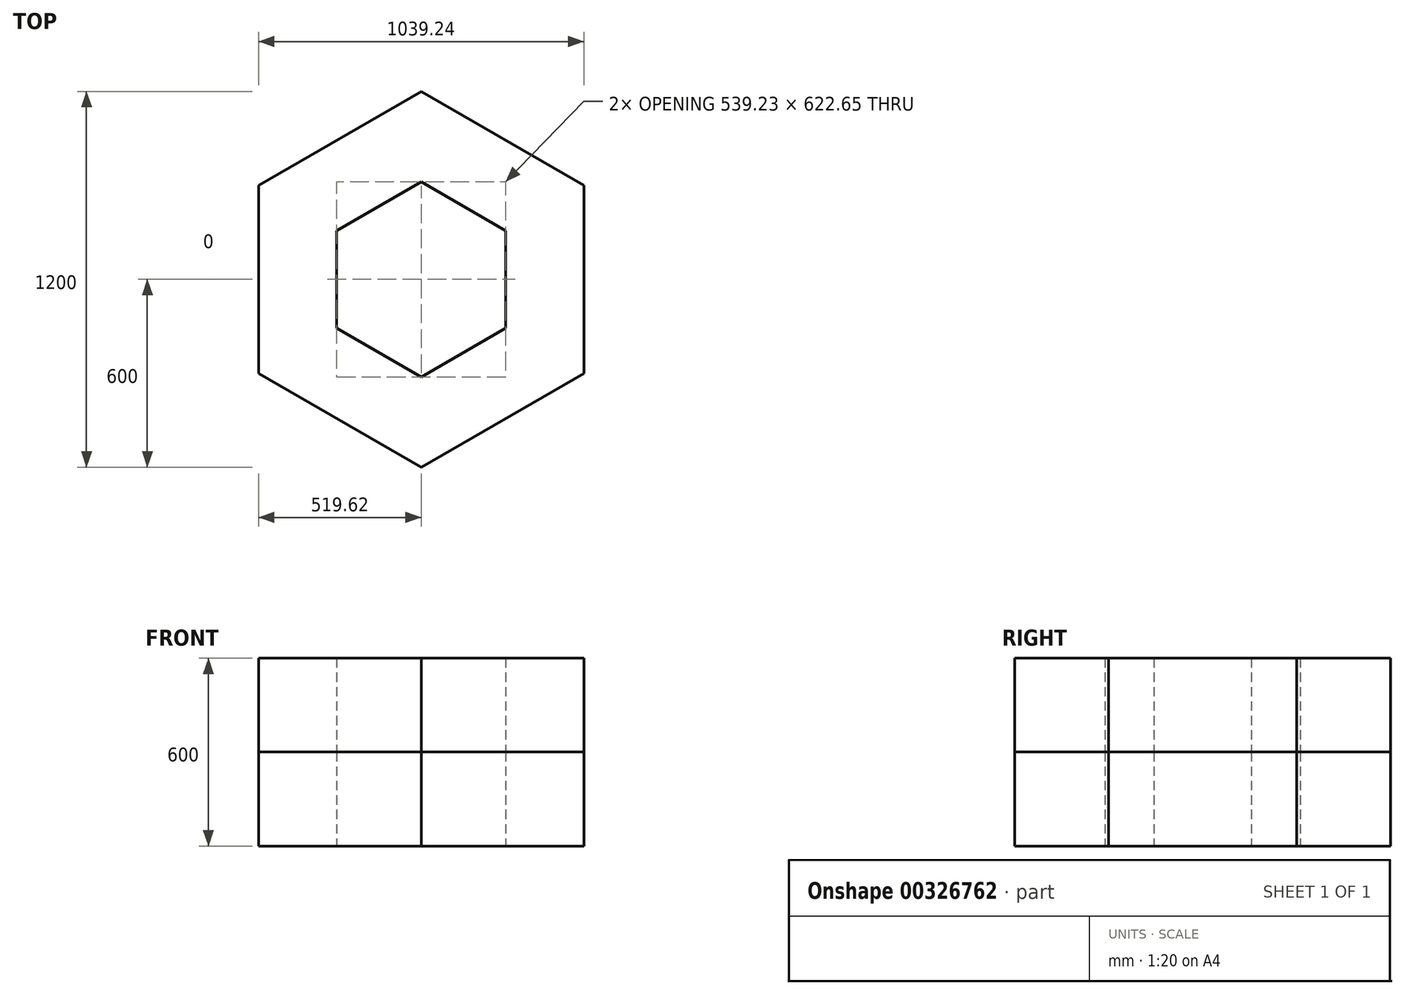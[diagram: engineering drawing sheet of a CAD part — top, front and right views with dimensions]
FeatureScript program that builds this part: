
annotation { "Feature Type Name" : "Feature", "Feature Type Description" : "" }
export const myFeature = defineFeature(function(context is Context, id is Id, definition is map)
    precondition{}
    {
        {
            var Q0;
            Q0=qCreatedBy(makeId("Top.planeOp"),FACE);
            var sketch = newSketch(context, id + "F0", { "sketchPlane" : qUnion([Q0])});
            skCircle(sketch, "E0.cCircle", {"center": v(0, 0) * mm, "radius": 519.62 * mm, "construction": true});
            skLineSegment(sketch, "E0.0", {"start": v(519.62, 300) * mm, "end": v(519.62, -300) * mm});
            skLineSegment(sketch, "E0.1", {"start": v(519.62, -300) * mm, "end": v(0, -600) * mm});
            skLineSegment(sketch, "E0.2", {"start": v(0, -600) * mm, "end": v(-519.62, -300) * mm});
            skLineSegment(sketch, "E0.3", {"start": v(-519.62, -300) * mm, "end": v(-519.62, 300) * mm});
            skLineSegment(sketch, "E0.4", {"start": v(-519.62, 300) * mm, "end": v(0, 600) * mm});
            skLineSegment(sketch, "E0.5", {"start": v(0, 600) * mm, "end": v(519.62, 300) * mm});
            skPoint(sketch, "E0.0.midPoint", {"position": v(519.62, 0) * mm});
            skCircle(sketch, "E1.cCircle", {"center": v(0, 0) * mm, "radius": 269.62 * mm, "construction": true});
            skLineSegment(sketch, "E1.0", {"start": v(269.62, 155.66) * mm, "end": v(269.62, -155.66) * mm});
            skLineSegment(sketch, "E1.1", {"start": v(269.62, -155.66) * mm, "end": v(0, -311.32) * mm});
            skLineSegment(sketch, "E1.2", {"start": v(0, -311.32) * mm, "end": v(-269.62, -155.66) * mm});
            skLineSegment(sketch, "E1.3", {"start": v(-269.62, -155.66) * mm, "end": v(-269.62, 155.66) * mm});
            skLineSegment(sketch, "E1.4", {"start": v(-269.62, 155.66) * mm, "end": v(0, 311.32) * mm});
            skLineSegment(sketch, "E1.5", {"start": v(0, 311.32) * mm, "end": v(269.62, 155.66) * mm});
            skPoint(sketch, "E1.0.midPoint", {"position": v(269.62, 0) * mm});
            skLineSegment(sketch, "E2", {"start": v(-519.62, -300) * mm, "end": v(-269.62, -155.66) * mm});
            skLineSegment(sketch, "E3", {"start": v(-519.62, 300) * mm, "end": v(-269.62, 155.66) * mm});
            skLineSegment(sketch, "E4", {"start": v(0, 311.32) * mm, "end": v(0, 600) * mm});
            skLineSegment(sketch, "E5", {"start": v(269.62, 155.66) * mm, "end": v(519.62, 300) * mm});
            skLineSegment(sketch, "E6", {"start": v(269.62, -155.66) * mm, "end": v(519.62, -300) * mm});
            skLineSegment(sketch, "E7", {"start": v(0, -600) * mm, "end": v(0, -311.32) * mm});
            skSolve(sketch);
        }
        {
            var Q0;
            Q0 = qSketchRegion(id + "F0", true);
            extrude(context, id + "F1", {"entities" : qUnion([Q0]), "depth" : 300 * mm});
        }
        {
            var Q0;
            Q0=makeQuery(id+"F1.opExtrude","SWEPT_BODY",BODY,{"disambiguationData":[OSD([sQuery(id+"F0.wireOp",EDGE,"E0.0"),sQuery(id+"F0.wireOp",EDGE,"E0.1"),sQuery(id+"F0.wireOp",EDGE,"E0.2"),sQuery(id+"F0.wireOp",EDGE,"E0.3"),sQuery(id+"F0.wireOp",EDGE,"E0.4"),sQuery(id+"F0.wireOp",EDGE,"E0.5"),sQuery(id+"F0.wireOp",EDGE,"E1.0"),sQuery(id+"F0.wireOp",EDGE,"E1.1"),sQuery(id+"F0.wireOp",EDGE,"E1.2"),sQuery(id+"F0.wireOp",EDGE,"E1.3"),sQuery(id+"F0.wireOp",EDGE,"E1.4"),sQuery(id+"F0.wireOp",EDGE,"E1.5")])]});
            transform(context, id + "F2", {"entities" : qUnion([Q0]), "transformType" : TransformType.TRANSLATION_3D, "dx" : 0 * mm, "dy" : 0 * mm, "dz" : 300 * mm, "makeCopy" : true});
        }
    });
